# Revit family: HVAC_Mechanical-Ventilation_Ice-Air_HWCAC_Vertical-Stack
name_source: partatom
category: Mechanical Equipment
revit_build: Autodesk Revit 2015 (Build: 20140606_1530(x64)
units: mm (PartAtom-declared; Revit-internal decimal feet)

## types (7) — shared parameters
Aluminum Material = Aluminum - Ice_Air - White
BIMobject category = Air Conditioning
BIMobject category code = hvac-air-con
BIMobject main category = HVAC
BIMobject main category code = hvac
Brand url = http://www.ice-air.com
Condensate Connection = 0.75 "
Date of publishing = 1/30/2014
Default Elevation = 48 "
Description = ICE AIRs Vertical Stack Hybrid Water-Cooled Air Conditioner (VSHW) provides an ideal solution for whisper quiet cooling and heating within a tight footprint.
Design country = United States
Edition number = 1
Floor Offset = 6 "
Frequency = 60 Hz
Front Panel Height = 60.5 "
Height = 88 "
IFC Classification = Heat Exchanger
Manufacturer = Ice Air
Manufacturer country = United States
Manufacturer name = Ice Air
Masterformat 2014 Code = 23 00 00
Masterformat 2014 Description = Heating, Ventilating, and Air Conditioning (HVAC)
NBS Reference Code = 03-03
NBS Reference Description = Air Conditioning Units
OmniClass Code = 23-33 39 11
OmniClass Description = Air Conditioners
Phase = 1
Plastic Material = Plastic - Ice_Air - White
Product Guid = 92ba711f-ba8b-42dc-a6e9-9ffb673129c2
Product SKU = vertical_stack_wshp_hybrid
Product data url = https://bimobject.com
Product family = Hybrid WCAC
Product group = Vertical Stack
Product url = http://www.ice-air.com
QR code = http://bimobject.com
Steel Material = Steel - Ice_Air - Galvanized
Technical description = http://www.ice-air.com
UNSPSC Code = 40101701
URL = http://www.ice-air.com
Uniclass 1.4 Code = JU
Uniclass 1.4 Description = Ventilation and air conditioning systems
Uniclass 2.0 Code = PR-03-03
Uniclass 2.0 Description = Air Conditioning Units
Uniclass 2015 Code = EF_65_80
Uniclass 2015 Name = Air conditioning
Uniformat II Code = D3090
Uniformat II Description = Other HVAC Systems & Equipment
Voltage = 230 V
Voltage (Range) = 208 - 230 V
Weight Net (Kg) = 0
zero-valued in all types: Nominal height, Nominal width

## per-type parameters (varying)
| type | Air Flow | Depth | Discharge Width | Energy Efficiency Rating w/ECM | Energy Efficiency Rating w/PSC | Flow Rate | Inlet/Outlet Connection | Top Duct Height | Top Duct Width | Total Cooling Capacity @ 86F EWT | Total Heating Capacity @ 105F EWT | Total Heating Capacity @ 120F EWT | Total Heating Capacity @ 95F EWT | Weight | Width | z Type |
| 8VSHW09 | 420 CFM | 17 " | 12 " | 14.7 | 14 | 2 GPM | 0.5 " | 12 " | 12 " | 9500.0 Btu/h | 8900.0 Btu/h | 12500.0 Btu/h | 6500.0 Btu/h | 156.00 lbm | 16 " | 1 |
| 8VSHW12 | 500 CFM | 17 " | 12 " | 14.8 | 13.7 | 3 GPM | 0.5 " | 12 " | 12 " | 13200.0 Btu/h | 12800.0 Btu/h | 13400.0 Btu/h | 12200.0 Btu/h | 156.00 lbm | 16 " | 2 |
| 8VSHW15 | 540 CFM | 17 " | 12 " | 15.3 | 14.4 | 4 GPM | 0.5 " | 12 " | 12 " | 13700.0 Btu/h | 14600.0 Btu/h | 16500.0 Btu/h | 13100.0 Btu/h | 156.00 lbm | 16 " | 3 |
| 8VSHW18 | 630 CFM | 20 " | 14 " | 15.2 | 14.4 | 5 GPM | 0.75 " | 14 " | 14 " | 17600.0 Btu/h | 15700.0 Btu/h | 18200.0 Btu/h | 14900.0 Btu/h | 183.00 lbm | 18 " | 4 |
| 8VSHW24 | 770 CFM | 20 " | 14 " | 14.1 | 13 | 6 GPM | 0.75 " | 14 " | 14 " | 22700.0 Btu/h | 23200.0 Btu/h | 29000.0 Btu/h | 22100.0 Btu/h | 183.00 lbm | 18 " | 5 |
| 8VSHW30 | 1000 CFM | 24 " | 18 " | 14.5 | 13.7 | 8 GPM | 0.75 " | 14 " | 18 " | 27800.0 Btu/h | 28800.0 Btu/h | 30200.0 Btu/h | 27300.0 Btu/h | 260.00 lbm | 22 " | 6 |
| 8VSHW36 | 1080 CFM | 24 " | 18 " | 13.9 | 13 | 9 GPM | 0.75 " | 14 " | 18 " | 36500.0 Btu/h | 29200.0 Btu/h | 37900.0 Btu/h | 27800.0 Btu/h | 264.00 lbm | 22 " | 7 |

note: column(s) folded — value = type name in every type: Model

## geometry (parser evidence)
native form markers: Sweep x6
no freeform markers — native parametric forms only
